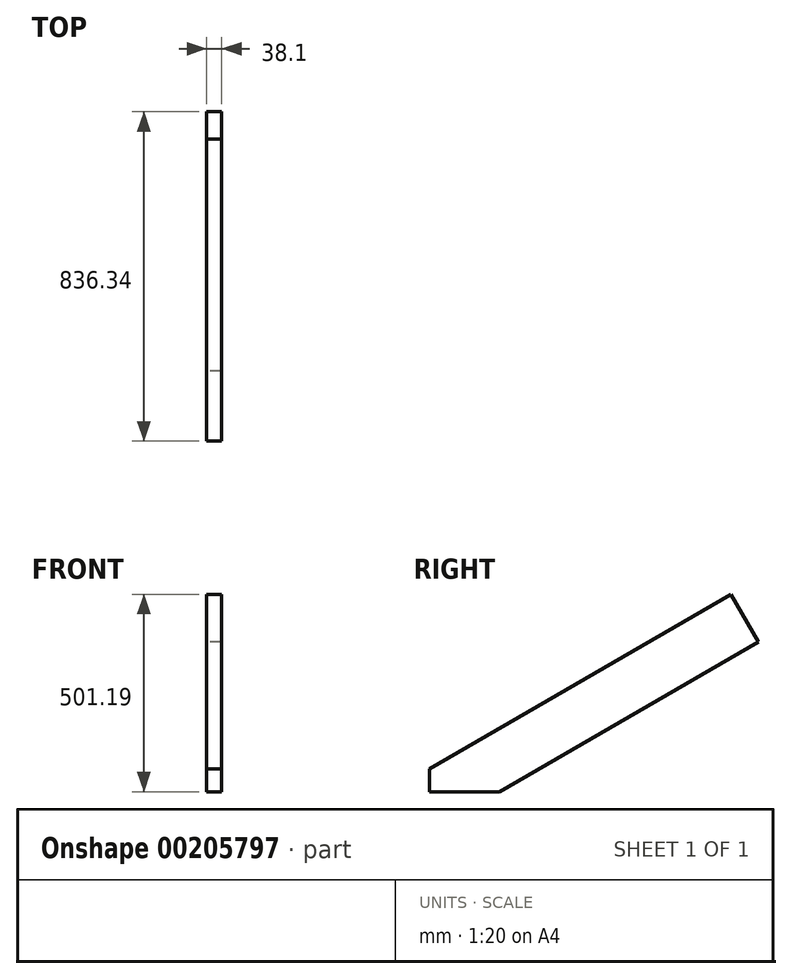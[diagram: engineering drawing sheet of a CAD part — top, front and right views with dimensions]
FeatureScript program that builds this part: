
annotation { "Feature Type Name" : "Feature", "Feature Type Description" : "" }
export const myFeature = defineFeature(function(context is Context, id is Id, definition is map)
    precondition{}
    {
        {
            var Q0;
            Q0=qCreatedBy(makeId("Right.planeOp"),FACE);
            var sketch = newSketch(context, id + "F0", { "sketchPlane" : qUnion([Q0])});
            skLineSegment(sketch, "E0", {"start": v(-3.36, -10.28) * mm, "end": v(-181.16, -10.28) * mm});
            skLineSegment(sketch, "E1", {"start": v(-181.16, -10.28) * mm, "end": v(-181.16, 48.37) * mm});
            skLineSegment(sketch, "E2", {"start": v(-181.16, 48.37) * mm, "end": v(585.33, 490.9) * mm});
            skLineSegment(sketch, "E3", {"start": v(585.33, 490.9) * mm, "end": v(655.18, 369.93) * mm});
            skLineSegment(sketch, "E4", {"start": v(655.18, 369.93) * mm, "end": v(-3.36, -10.28) * mm});
            skSolve(sketch);
        }
        {
            var Q0;
            Q0 = qSketchRegion(id + "F0", true);
            extrude(context, id + "F1", {"entities" : qUnion([Q0]), "depth" : 38.1 * mm});
        }
    });
